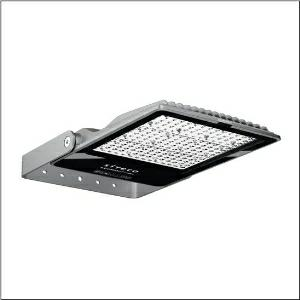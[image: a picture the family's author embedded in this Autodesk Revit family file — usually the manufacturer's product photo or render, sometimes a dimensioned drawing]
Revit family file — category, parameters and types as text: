
# Revit family: sicompact_r__31_midi___pl32_5xa7581e1k23_f752
name_source: partatom
category: Lighting Fixtures
units: mm (PartAtom-declared; Revit-internal decimal feet)

## family parameters
Cut with Voids When Loaded = No
Host = Face
Light Source = No
Part Type = Normal
Room Calculation Point = No
Round Connector Dimension = Use Diameter
Shared = No

## types (1)
- SiCompact® 31 midi  PL32 (1 x LED, 37000 lm, 250 W, 3000K)
    Apparent Load = 250 VA
    CIE Flux Codes = 32 69 98 100 100
    Color Rendering = 70
    Color Temperature = 3000K
    Default Elevation = 1800 mm
    Description = SiCompact® 31 midi, floodlight, primary light control with lens, of plastic, of toughened safety glass, transparent, light distribution: PL32, light emission: direct distribution, primary light characteristic: asymmetric, installation type: surface-mounted, LED, High Power LED, rated luminous flux: 37.000lm, luminous efficacy: 148lm/W, light colour: 730, colour temperature: 3000K, control gear: ECG, with cable, 3x 1.5mm², mains connection: 220..240V, AC, 50/60Hz, connection cable pre-assembled, cable length: 2m, rated input power: 250W, of diecast aluminium, specular, metallic grey (RAL 9006), length: 560mm, width: 330mm, height: 62mm, bracket, of sheet steel, coated, metallic grey (RAL 9006), ON/OFF, protection rating (complete): IP66, insulation class (complete): insulation class I (protective earthing), certification: CE, impact resistance: IK08, permissible operating ambient temperature: -40..+45°C, packaging unit: 1 piece

Light Distribution: PL32
    Height = 62 mm  [stored 0.203412 ft]
    Lamp = 1 x LED
    Lamp Light Flux = 37000 lm
    Lamp Power = 250 W
    Lamp count = 1
    Length = 560 mm
    Luminous efficacy = 148 lm/W
    Manufacturer = Siteco
    ModVariant = No
    Model = 5XA7581E1K23
    Number of Poles = 1
    OnlyDefault = Yes
    Power Factor = 1
    Product Name = SiCompact® 31 midi | PL32
    Product group = floodlight | pylon top
    ProductGroupID = 6101
    Protection Class = Protection class I
    Protection Degree = IP 66
    RLX_Detail_Level = 1
    RlxData = <blob elided: 98297 chars, md5=743d0912>
    Socket = socket
    Standby Power = 0 W
    System Light Flux = 37000 lm
    System Power = 250 W
    Type Comments = Product without accessories
    Type Image = l_1006415.jpg
    URL = http://relux.com
    VarID = ---
    Voltage = 0 V
    Weight = 0.00 kg
    Width = 333 mm

note: [stored X ft] marks values corroborated as IEEE doubles in the binary element streams (Revit-internal decimal feet)

## geometry (parser evidence)
native form markers: Blend x4, Sweep x13
no freeform markers — native parametric forms only
